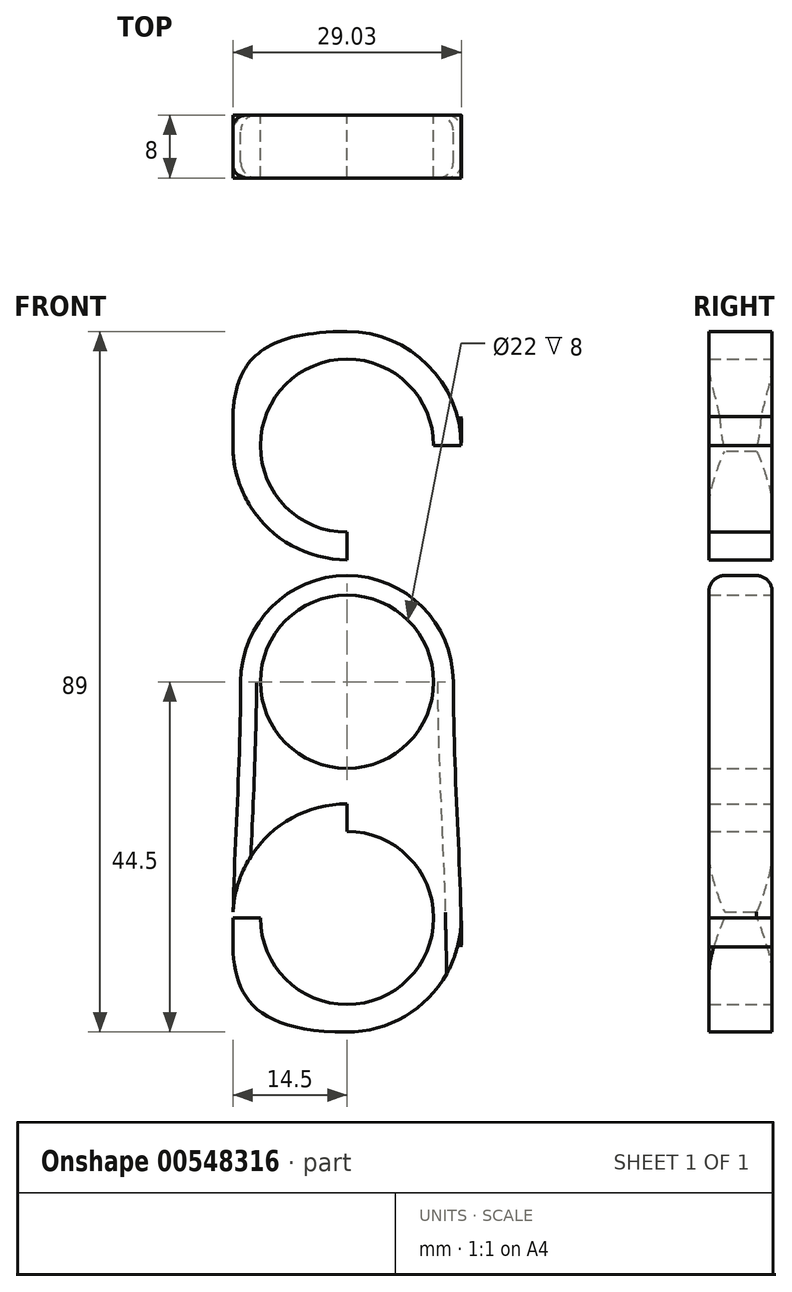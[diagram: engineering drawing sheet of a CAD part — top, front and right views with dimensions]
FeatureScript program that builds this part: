
annotation { "Feature Type Name" : "Feature", "Feature Type Description" : "" }
export const myFeature = defineFeature(function(context is Context, id is Id, definition is map)
    precondition{}
    {
        {
            var Q0;
            Q0=qCreatedBy(makeId("Front.planeOp"),FACE);
            var sketch = newSketch(context, id + "F0", { "sketchPlane" : qUnion([Q0])});
            skCircle(sketch, "E0", {"center": v(0, 0) * mm, "radius": 13.5 * mm});
            skLineSegment(sketch, "E1", {"start": v(0, 30) * mm, "end": v(0, -30) * mm});
            skCircle(sketch, "E2", {"center": v(0, 30) * mm, "radius": 14.5 * mm});
            skCircle(sketch, "E3", {"center": v(0, -30) * mm, "radius": 14.5 * mm});
            skLineSegment(sketch, "E4", {"start": v(0, 44.5) * mm, "end": v(0, -44.5) * mm});
            skLineSegment(sketch, "E5", {"start": v(0, 30) * mm, "end": v(-14.5, 30) * mm});
            skLineSegment(sketch, "E6", {"start": v(0, -30) * mm, "end": v(-14.5, -30) * mm});
            skLineSegment(sketch, "E7", {"start": v(0, 30) * mm, "end": v(14.5, 30) * mm});
            skLineSegment(sketch, "E8", {"start": v(0, -30) * mm, "end": v(14.5, -30) * mm});
            skFitSpline(sketch, "E9", {"points": [v(0, 44.5) * mm, v(-14.5, 30) * mm, v(-13.5, 0) * mm, v(-14.5, -30) * mm, v(0, -44.5) * mm], "startDerivative": vector(-192.26, 0) * mm, "endDerivative": vector(192.26, 0) * mm});
            skFitSpline(sketch, "E10", {"points": [v(0, -44.5) * mm, v(14.5, -30) * mm, v(13.5, 0) * mm, v(14.5, 30) * mm, v(0, 44.5) * mm], "startDerivative": vector(192.26, 0) * mm, "endDerivative": vector(-192.26, 0) * mm});
            skCircle(sketch, "E11", {"center": v(0, -30) * mm, "radius": 11 * mm});
            skCircle(sketch, "E12", {"center": v(0, 30) * mm, "radius": 11 * mm});
            skLineSegment(sketch, "E13", {"start": v(-14.5, 44.5) * mm, "end": v(-14.5, -44.5) * mm});
            skLineSegment(sketch, "E14", {"start": v(14.5, -44.5) * mm, "end": v(14.5, 44.5) * mm});
            skCircle(sketch, "E15", {"center": v(0, 0) * mm, "radius": 11 * mm});
            skSolve(sketch);
        }
        {
            var Q0;
            {var subQ0=sQuery(id+"F0.wireOp",EDGE,"E10");var subQ3=sQuery(id+"F0.wireOp",EDGE,"E14");var subQ5=makeQuery(id+"F0.imprint","INTERSECT",VERTEX,{"disambiguationData":[OD(1.0)],"derivedFrom":[subQ0,subQ3]});Q0=makeQuery(id+"F0.imprint","IMPRINT",FACE,{"disambiguationData":[TD([[makeQuery(id+"F0.imprint","IMPRINT",EDGE,{"disambiguationData":[TD([[subQ5,-1.0]])],"derivedFrom":subQ0}),1.0]])]});}
            var Q1;
            {var subQ1=sQuery(id+"F0.wireOp",EDGE,"E4");var subQ6=sQuery(id+"F0.wireOp",EDGE,"E12");var subQ8=makeQuery(id+"F0.imprint","INTERSECT",VERTEX,{"disambiguationData":[OD(0.0)],"derivedFrom":[subQ1,subQ6]});Q1=makeQuery(id+"F0.imprint","IMPRINT",FACE,{"disambiguationData":[TD([[makeQuery(id+"F0.imprint","IMPRINT",EDGE,{"disambiguationData":[TD([[subQ8,1.0]])],"derivedFrom":subQ6}),-1.0]])]});}
            var Q2;
            {var subQ1=sQuery(id+"F0.wireOp",EDGE,"E4");var subQ6=sQuery(id+"F0.wireOp",EDGE,"E12");var subQ8=makeQuery(id+"F0.imprint","INTERSECT",VERTEX,{"disambiguationData":[OD(0.0)],"derivedFrom":[subQ1,subQ6]});Q2=makeQuery(id+"F0.imprint","IMPRINT",FACE,{"disambiguationData":[TD([[makeQuery(id+"F0.imprint","IMPRINT",EDGE,{"disambiguationData":[TD([[subQ8,-1.0]])],"derivedFrom":subQ6}),-1.0]])]});}
            var Q3;
            {var subQ0=sQuery(id+"F0.wireOp",EDGE,"E9");var subQ3=sQuery(id+"F0.wireOp",EDGE,"E13");var subQ5=makeQuery(id+"F0.imprint","INTERSECT",VERTEX,{"disambiguationData":[OD(0.0)],"derivedFrom":[subQ0,subQ3]});Q3=makeQuery(id+"F0.imprint","IMPRINT",FACE,{"disambiguationData":[TD([[makeQuery(id+"F0.imprint","IMPRINT",EDGE,{"disambiguationData":[TD([[subQ5,1.0]])],"derivedFrom":subQ0}),1.0]])]});}
            var Q4;
            {var subQ0=sQuery(id+"F0.wireOp",EDGE,"E9");var subQ2=sQuery(id+"F0.wireOp",EDGE,"E2");var subQ9=makeQuery(id+"F0.imprint","INTERSECT",VERTEX,{"derivedFrom":[subQ2,subQ0]});Q4=makeQuery(id+"F0.imprint","IMPRINT",FACE,{"disambiguationData":[TD([[makeQuery(id+"F0.imprint","IMPRINT",EDGE,{"disambiguationData":[TD([[subQ9,-1.0]])],"derivedFrom":subQ2}),1.0]])]});}
            var Q5;
            {var subQ0=sQuery(id+"F0.wireOp",EDGE,"E4");var subQ1=sQuery(id+"F0.wireOp",EDGE,"E0");var subQ2=makeQuery(id+"F0.imprint","INTERSECT",VERTEX,{"disambiguationData":[OD(0.0)],"derivedFrom":[subQ1,subQ0]});Q5=makeQuery(id+"F0.imprint","IMPRINT",FACE,{"disambiguationData":[TD([[makeQuery(id+"F0.imprint","IMPRINT",EDGE,{"disambiguationData":[TD([[subQ2,-1.0]])],"derivedFrom":subQ1}),-1.0]])]});}
            var Q6;
            {var subQ2=sQuery(id+"F0.wireOp",EDGE,"E2");var subQ7=sQuery(id+"F0.wireOp",EDGE,"E4");var subQ8=makeQuery(id+"F0.imprint","INTERSECT",VERTEX,{"derivedFrom":[subQ2,subQ7]});Q6=makeQuery(id+"F0.imprint","IMPRINT",FACE,{"disambiguationData":[TD([[makeQuery(id+"F0.imprint","IMPRINT",EDGE,{"disambiguationData":[TD([[subQ8,-1.0]])],"derivedFrom":subQ2}),1.0]])]});}
            var Q7;
            {var subQ0=sQuery(id+"F0.wireOp",EDGE,"E4");var subQ1=sQuery(id+"F0.wireOp",EDGE,"E0");var subQ2=makeQuery(id+"F0.imprint","INTERSECT",VERTEX,{"disambiguationData":[OD(0.0)],"derivedFrom":[subQ1,subQ0]});Q7=makeQuery(id+"F0.imprint","IMPRINT",FACE,{"disambiguationData":[TD([[makeQuery(id+"F0.imprint","IMPRINT",EDGE,{"disambiguationData":[TD([[subQ2,1.0]])],"derivedFrom":subQ1}),-1.0]])]});}
            var Q8;
            {var subQ0=sQuery(id+"F0.wireOp",EDGE,"E4");var subQ1=sQuery(id+"F0.wireOp",EDGE,"E0");var subQ2=makeQuery(id+"F0.imprint","INTERSECT",VERTEX,{"disambiguationData":[OD(0.0)],"derivedFrom":[subQ1,subQ0]});Q8=makeQuery(id+"F0.imprint","IMPRINT",FACE,{"disambiguationData":[TD([[makeQuery(id+"F0.imprint","IMPRINT",EDGE,{"disambiguationData":[TD([[subQ2,1.0]])],"derivedFrom":subQ1}),1.0]])]});}
            var Q9;
            {var subQ0=sQuery(id+"F0.wireOp",EDGE,"E4");var subQ1=sQuery(id+"F0.wireOp",EDGE,"E0");var subQ5=makeQuery(id+"F0.imprint","INTERSECT",VERTEX,{"disambiguationData":[OD(0.0)],"derivedFrom":[subQ1,subQ0]});Q9=makeQuery(id+"F0.imprint","IMPRINT",FACE,{"disambiguationData":[TD([[makeQuery(id+"F0.imprint","IMPRINT",EDGE,{"disambiguationData":[TD([[subQ5,-1.0]])],"derivedFrom":subQ1}),1.0]])]});}
            var Q10;
            {var subQ0=sQuery(id+"F0.wireOp",EDGE,"E10");var subQ1=sQuery(id+"F0.wireOp",EDGE,"E0");var subQ2=makeQuery(id+"F0.imprint","INTERSECT",VERTEX,{"derivedFrom":[subQ1,subQ0]});Q10=makeQuery(id+"F0.imprint","IMPRINT",FACE,{"disambiguationData":[TD([[makeQuery(id+"F0.imprint","IMPRINT",EDGE,{"disambiguationData":[TD([[subQ2,1.0]])],"derivedFrom":subQ1}),-1.0]])]});}
            var Q11;
            {var subQ0=sQuery(id+"F0.wireOp",EDGE,"E10");var subQ2=sQuery(id+"F0.wireOp",EDGE,"E3");var subQ4=makeQuery(id+"F0.imprint","INTERSECT",VERTEX,{"derivedFrom":[subQ2,subQ0]});Q11=makeQuery(id+"F0.imprint","IMPRINT",FACE,{"disambiguationData":[TD([[makeQuery(id+"F0.imprint","IMPRINT",EDGE,{"disambiguationData":[TD([[subQ4,-1.0]])],"derivedFrom":subQ2}),1.0]])]});}
            var Q12;
            {var subQ0=sQuery(id+"F0.wireOp",EDGE,"E4");var subQ1=sQuery(id+"F0.wireOp",EDGE,"E3");var subQ2=makeQuery(id+"F0.imprint","INTERSECT",VERTEX,{"derivedFrom":[subQ1,subQ0]});Q12=makeQuery(id+"F0.imprint","IMPRINT",FACE,{"disambiguationData":[TD([[makeQuery(id+"F0.imprint","IMPRINT",EDGE,{"disambiguationData":[TD([[subQ2,-1.0]])],"derivedFrom":subQ1}),1.0]])]});}
            var Q13;
            {var subQ0=sQuery(id+"F0.wireOp",EDGE,"E9");var subQ1=sQuery(id+"F0.wireOp",EDGE,"E0");var subQ2=makeQuery(id+"F0.imprint","INTERSECT",VERTEX,{"derivedFrom":[subQ1,subQ0]});Q13=makeQuery(id+"F0.imprint","IMPRINT",FACE,{"disambiguationData":[TD([[makeQuery(id+"F0.imprint","IMPRINT",EDGE,{"disambiguationData":[TD([[subQ2,-1.0]])],"derivedFrom":subQ1}),-1.0]])]});}
            var Q14;
            {var subQ1=sQuery(id+"F0.wireOp",EDGE,"E4");var subQ6=sQuery(id+"F0.wireOp",EDGE,"E11");var subQ7=makeQuery(id+"F0.imprint","INTERSECT",VERTEX,{"disambiguationData":[OD(1.0)],"derivedFrom":[subQ1,subQ6]});Q14=makeQuery(id+"F0.imprint","IMPRINT",FACE,{"disambiguationData":[TD([[makeQuery(id+"F0.imprint","IMPRINT",EDGE,{"disambiguationData":[TD([[subQ7,1.0]])],"derivedFrom":subQ6}),-1.0]])]});}
            var Q15;
            {var subQ0=sQuery(id+"F0.wireOp",EDGE,"E9");var subQ3=sQuery(id+"F0.wireOp",EDGE,"E13");var subQ5=makeQuery(id+"F0.imprint","INTERSECT",VERTEX,{"disambiguationData":[OD(1.0)],"derivedFrom":[subQ0,subQ3]});Q15=makeQuery(id+"F0.imprint","IMPRINT",FACE,{"disambiguationData":[TD([[makeQuery(id+"F0.imprint","IMPRINT",EDGE,{"disambiguationData":[TD([[subQ5,-1.0]])],"derivedFrom":subQ0}),1.0]])]});}
            var Q16;
            {var subQ0=sQuery(id+"F0.wireOp",EDGE,"E10");var subQ3=sQuery(id+"F0.wireOp",EDGE,"E14");var subQ5=makeQuery(id+"F0.imprint","INTERSECT",VERTEX,{"disambiguationData":[OD(0.0)],"derivedFrom":[subQ0,subQ3]});Q16=makeQuery(id+"F0.imprint","IMPRINT",FACE,{"disambiguationData":[TD([[makeQuery(id+"F0.imprint","IMPRINT",EDGE,{"disambiguationData":[TD([[subQ5,1.0]])],"derivedFrom":subQ0}),1.0]])]});}
            var Q17;
            {var subQ1=sQuery(id+"F0.wireOp",EDGE,"E4");var subQ6=sQuery(id+"F0.wireOp",EDGE,"E11");var subQ7=makeQuery(id+"F0.imprint","INTERSECT",VERTEX,{"disambiguationData":[OD(1.0)],"derivedFrom":[subQ1,subQ6]});Q17=makeQuery(id+"F0.imprint","IMPRINT",FACE,{"disambiguationData":[TD([[makeQuery(id+"F0.imprint","IMPRINT",EDGE,{"disambiguationData":[TD([[subQ7,-1.0]])],"derivedFrom":subQ6}),-1.0]])]});}
            extrude(context, id + "F1", {"entities" : qUnion([Q0, Q1, Q2, Q3, Q4, Q5, Q6, Q7, Q8, Q9, Q10, Q11, Q12, Q13, Q14, Q15, Q16, Q17]), "depth" : 8 * mm, "offsetDistance" : 25.4 * mm});
        }
        {
            var Q0;
            {var subQ1=sQuery(id+"F0.wireOp",EDGE,"E10");var subQ2=sQuery(id+"F0.wireOp",EDGE,"E2");var subQ3=makeQuery(id+"F0.imprint","INTERSECT",VERTEX,{"derivedFrom":[subQ2,subQ1]});var subQ4=makeQuery(id+"F0.imprint","INTERSECT",VERTEX,{"derivedFrom":[sQuery(id+"F0.wireOp",EDGE,"E0"),subQ1]});var subQ5=sQuery(id+"F0.wireOp",EDGE,"E3");var subQ6=makeQuery(id+"F0.imprint","INTERSECT",VERTEX,{"derivedFrom":[subQ5,subQ1]});Q0=makeQuery(id+"F1.opExtrude","CAP_EDGE",EDGE,{"disambiguationData":[OSD([subQ1]),TDD([makeQuery(id+"F0.imprint","IMPRINT",EDGE,{"disambiguationData":[TD([[subQ6,1.0]])],"derivedFrom":subQ1}),makeQuery(id+"F0.imprint","IMPRINT",EDGE,{"disambiguationData":[TD([[subQ4,1.0]])],"derivedFrom":subQ1}),makeQuery(id+"F0.imprint","IMPRINT",EDGE,{"disambiguationData":[TD([[subQ4,-1.0]])],"derivedFrom":subQ1}),makeQuery(id+"F0.imprint","IMPRINT",EDGE,{"disambiguationData":[TD([[subQ3,-1.0]])],"derivedFrom":subQ1})])],"isStart":false});}
            var Q1;
            {var subQ1=sQuery(id+"F0.wireOp",EDGE,"E9");var subQ2=sQuery(id+"F0.wireOp",EDGE,"E3");var subQ3=makeQuery(id+"F0.imprint","INTERSECT",VERTEX,{"derivedFrom":[subQ2,subQ1]});var subQ4=makeQuery(id+"F0.imprint","INTERSECT",VERTEX,{"derivedFrom":[sQuery(id+"F0.wireOp",EDGE,"E0"),subQ1]});var subQ5=sQuery(id+"F0.wireOp",EDGE,"E2");var subQ6=makeQuery(id+"F0.imprint","INTERSECT",VERTEX,{"derivedFrom":[subQ5,subQ1]});Q1=makeQuery(id+"F1.opExtrude","CAP_EDGE",EDGE,{"disambiguationData":[OSD([subQ1]),TDD([makeQuery(id+"F0.imprint","IMPRINT",EDGE,{"disambiguationData":[TD([[subQ6,1.0]])],"derivedFrom":subQ1}),makeQuery(id+"F0.imprint","IMPRINT",EDGE,{"disambiguationData":[TD([[subQ4,1.0]])],"derivedFrom":subQ1}),makeQuery(id+"F0.imprint","IMPRINT",EDGE,{"disambiguationData":[TD([[subQ4,-1.0]])],"derivedFrom":subQ1}),makeQuery(id+"F0.imprint","IMPRINT",EDGE,{"disambiguationData":[TD([[subQ3,-1.0]])],"derivedFrom":subQ1})])],"isStart":false});}
            var Q2;
            {var subQ1=sQuery(id+"F0.wireOp",EDGE,"E10");var subQ2=sQuery(id+"F0.wireOp",EDGE,"E2");var subQ3=makeQuery(id+"F0.imprint","INTERSECT",VERTEX,{"derivedFrom":[subQ2,subQ1]});var subQ4=makeQuery(id+"F0.imprint","INTERSECT",VERTEX,{"derivedFrom":[sQuery(id+"F0.wireOp",EDGE,"E0"),subQ1]});var subQ5=sQuery(id+"F0.wireOp",EDGE,"E3");var subQ6=makeQuery(id+"F0.imprint","INTERSECT",VERTEX,{"derivedFrom":[subQ5,subQ1]});Q2=makeQuery(id+"F1.opExtrude","CAP_EDGE",EDGE,{"disambiguationData":[OSD([subQ1]),TDD([makeQuery(id+"F0.imprint","IMPRINT",EDGE,{"disambiguationData":[TD([[subQ6,1.0]])],"derivedFrom":subQ1}),makeQuery(id+"F0.imprint","IMPRINT",EDGE,{"disambiguationData":[TD([[subQ4,1.0]])],"derivedFrom":subQ1}),makeQuery(id+"F0.imprint","IMPRINT",EDGE,{"disambiguationData":[TD([[subQ4,-1.0]])],"derivedFrom":subQ1}),makeQuery(id+"F0.imprint","IMPRINT",EDGE,{"disambiguationData":[TD([[subQ3,-1.0]])],"derivedFrom":subQ1})])],"isStart":true});}
            var Q3;
            {var subQ1=sQuery(id+"F0.wireOp",EDGE,"E9");var subQ2=sQuery(id+"F0.wireOp",EDGE,"E3");var subQ3=makeQuery(id+"F0.imprint","INTERSECT",VERTEX,{"derivedFrom":[subQ2,subQ1]});var subQ4=makeQuery(id+"F0.imprint","INTERSECT",VERTEX,{"derivedFrom":[sQuery(id+"F0.wireOp",EDGE,"E0"),subQ1]});var subQ5=sQuery(id+"F0.wireOp",EDGE,"E2");var subQ6=makeQuery(id+"F0.imprint","INTERSECT",VERTEX,{"derivedFrom":[subQ5,subQ1]});Q3=makeQuery(id+"F1.opExtrude","CAP_EDGE",EDGE,{"disambiguationData":[OSD([subQ1]),TDD([makeQuery(id+"F0.imprint","IMPRINT",EDGE,{"disambiguationData":[TD([[subQ6,1.0]])],"derivedFrom":subQ1}),makeQuery(id+"F0.imprint","IMPRINT",EDGE,{"disambiguationData":[TD([[subQ4,1.0]])],"derivedFrom":subQ1}),makeQuery(id+"F0.imprint","IMPRINT",EDGE,{"disambiguationData":[TD([[subQ4,-1.0]])],"derivedFrom":subQ1}),makeQuery(id+"F0.imprint","IMPRINT",EDGE,{"disambiguationData":[TD([[subQ3,-1.0]])],"derivedFrom":subQ1})])],"isStart":true});}
            fillet(context, id + "F2", {"entities" : qUnion([Q0, Q1, Q2, Q3]), "radius" : 2 * mm, "tangentPropagation" : true, "allowEdgeOverflow" : false});
        }
    });
